# Revit family: Reece_Laundry Trough_Base_Laundry Trough and Cabinet_Double
name_source: partatom
category: Plumbing Fixtures
revit_build: Autodesk Revit 2018 (Build: 20180329_1100(x64)
units: mm (PartAtom-declared; Revit-internal decimal feet)

## family parameters
Always vertical = Yes
Cut with Voids When Loaded = No
Part Type = Normal
Room Calculation Point = Yes
Round Connector Dimension = Use Diameter
Shared = Yes
Work Plane-Based = No

## types (1)
- 90 Litres_Stainless Steel_2 Doors_White
    Description = Base Double Laundry Trough & Cabinet 1 Taphole 45 litres Stainless Steel/ White
    Disclaimer = THIS FILE IS THE PROPERTY OF THE REECE GROUP. IT MAY NOT BE REPRODUCED, REVERSE-ENGINEERED OR MODIFIED. ANY REPUBLICATION, TRANSMISSION OR DISTRIBUTION FOR THE PURPOSE OF COMMERCIALLY EXPLOITING THE FILES IS PROHIBITED.
    Keynote = Product #9504722, Reece_Laundry Trough_Base_Laundry Trough and Cabinet_Double - 90 Litres_Stainless Steel_2 Doors_White
    Manufacturer = Base
    Model = -
    Reece_Detail_Additional = Double Trough
    Reece_Detail_Disclaimer = THIS FILE IS THE PROPERTY OF THE REECE GROUP. IT MAY NOT BE REPRODUCED, REVERSE-ENGINEERED OR MODIFIED. ANY REPUBLICATION, TRANSMISSION OR DISTRIBUTION FOR THE PURPOSE OF COMMERCIALLY EXPLOITING THE FILES IS PROHIBITED.
    Reece_Material-Cabinet = Reece_Acrylic_White
    Reece_Material_Main = Reece_Metal_Steel
    Reece_Material_Secondary = Reece_Metal_Steel
    Reece_Overall_Capacity = 90 L
    Reece_Overall_Height = 870 mm  [stored 2.85433 ft]
    Reece_Overall_Length = 500 mm  [stored 1.64042 ft]
    Reece_Overall_Width = 1160 mm  [stored 3.80577 ft]
    Reece_Product_Brand = Base
    Reece_Product_Description = Base Double Laundry Trough & Cabinet 1 Taphole 45 litres Stainless Steel/ White
    Reece_Product_Doors = 2
    Reece_Product_Mount = Floor Mounted
    Reece_Product_Number = 9504722
    Reece_Product_Sub Brand = -
    Reece_Product_Web Page = https://www.reece.com.au
    Reece_Sink_Outlet = 40 mm  [stored 0.131234 ft]
    URL = https://www.reece.com.au

note: [stored X ft] marks values corroborated as IEEE doubles in the binary element streams (Revit-internal decimal feet)

## geometry (parser evidence)
native form markers: Sweep x6
no freeform markers — native parametric forms only
